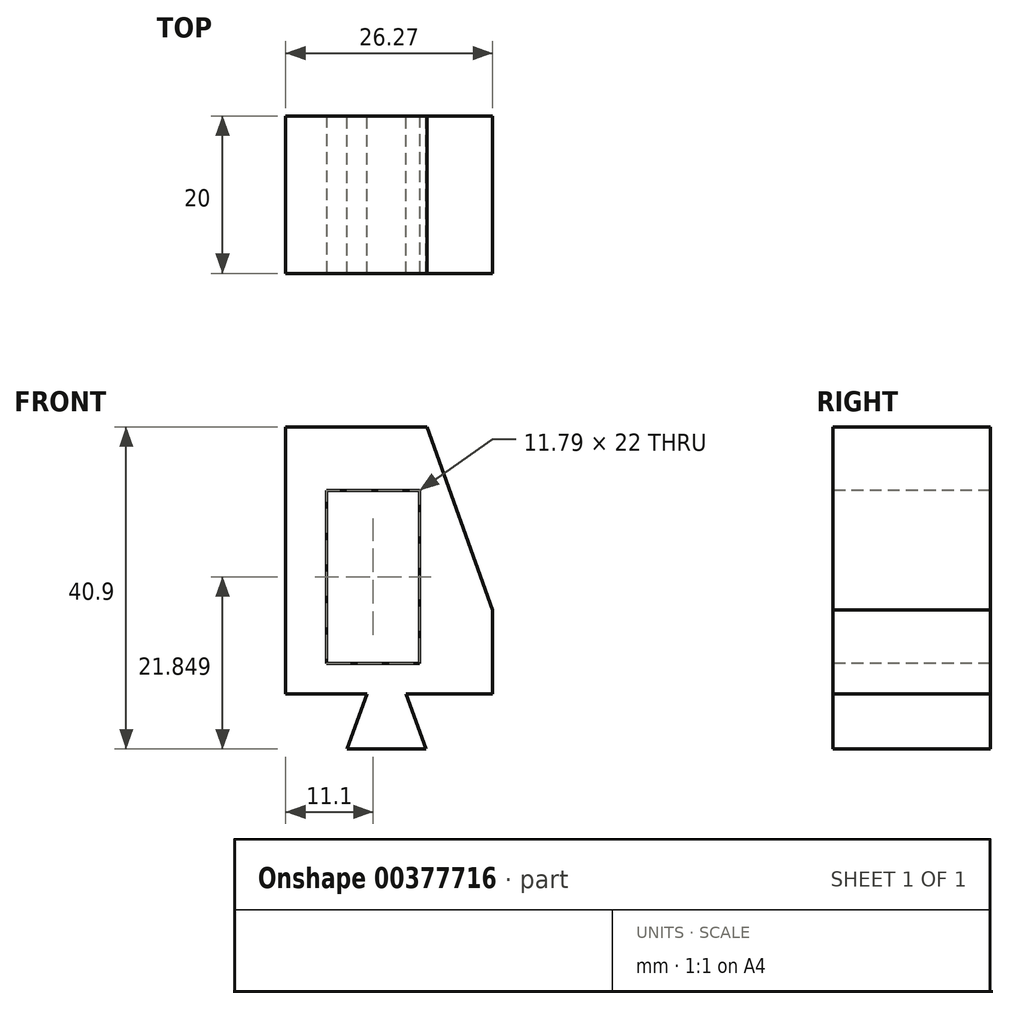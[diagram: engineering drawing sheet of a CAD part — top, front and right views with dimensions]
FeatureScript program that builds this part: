
annotation { "Feature Type Name" : "Feature", "Feature Type Description" : "" }
export const myFeature = defineFeature(function(context is Context, id is Id, definition is map)
    precondition{}
    {
        {
            var Q0;
            Q0=qCreatedBy(makeId("Front.planeOp"),FACE);
            var sketch = newSketch(context, id + "F0", { "sketchPlane" : qUnion([Q0])});
            skLineSegment(sketch, "E0", {"start": v(0, 0) * mm, "end": v(0, 4.85) * mm, "construction": true});
            skLineSegment(sketch, "E1", {"start": v(-5, -2.88) * mm, "end": v(5, -2.88) * mm});
            skLineSegment(sketch, "E2", {"start": v(5, -2.88) * mm, "end": v(2.48, 4.12) * mm});
            skLineSegment(sketch, "E3", {"start": v(2.48, 4.12) * mm, "end": v(13.47, 4.12) * mm});
            skLineSegment(sketch, "E4", {"start": v(13.47, 4.12) * mm, "end": v(13.47, 14.8) * mm});
            skLineSegment(sketch, "E5", {"start": v(-5, -2.88) * mm, "end": v(-2.48, 4.12) * mm});
            skLineSegment(sketch, "E6", {"start": v(-2.48, 4.12) * mm, "end": v(-12.8, 4.12) * mm});
            skLineSegment(sketch, "E7", {"start": v(13.47, 14.8) * mm, "end": v(5.18, 38.02) * mm});
            skLineSegment(sketch, "E8", {"start": v(5.18, 38.02) * mm, "end": v(-12.8, 38.02) * mm});
            skLineSegment(sketch, "E9", {"start": v(-12.8, 38.02) * mm, "end": v(-12.8, 4.12) * mm});
            skSolve(sketch);
        }
        {
            var Q0;
            Q0 = qSketchRegion(id + "F0", true);
            extrude(context, id + "F1", {"entities" : qUnion([Q0]), "endBound" : BoundingType.SYMMETRIC, "depth" : 20 * mm});
        }
        {
            var Q0;
            Q0=makeQuery(id+"F1.opExtrude","CAP_FACE",FACE,{"disambiguationData":[OSD([sQuery(id+"F0.wireOp",EDGE,"E1"),sQuery(id+"F0.wireOp",EDGE,"E2"),sQuery(id+"F0.wireOp",EDGE,"E3"),sQuery(id+"F0.wireOp",EDGE,"E4"),sQuery(id+"F0.wireOp",EDGE,"E5"),sQuery(id+"F0.wireOp",EDGE,"E6"),sQuery(id+"F0.wireOp",EDGE,"E7"),sQuery(id+"F0.wireOp",EDGE,"E8"),sQuery(id+"F0.wireOp",EDGE,"E9")])],"isStart":false});
            var sketch = newSketch(context, id + "F2", { "sketchPlane" : qUnion([Q0])});
            skLineSegment(sketch, "E10.bottom", {"start": v(-7.6, 29.97) * mm, "end": v(4.2, 29.97) * mm});
            skLineSegment(sketch, "E10.top", {"start": v(-7.6, 7.97) * mm, "end": v(4.2, 7.97) * mm});
            skLineSegment(sketch, "E10.left", {"start": v(-7.6, 29.97) * mm, "end": v(-7.6, 7.97) * mm});
            skLineSegment(sketch, "E10.right", {"start": v(4.2, 29.97) * mm, "end": v(4.2, 7.97) * mm});
            skSolve(sketch);
        }
        {
            var Q0;
            Q0 = qSketchRegion(id + "F2", true);
            extrude(context, id + "F3", {"entities" : qUnion([Q0]), "operationType" : NewBodyOperationType.REMOVE, "endBound" : BoundingType.THROUGH_ALL, "oppositeDirection" : true, "depth" : 25 * mm});
        }
    });
